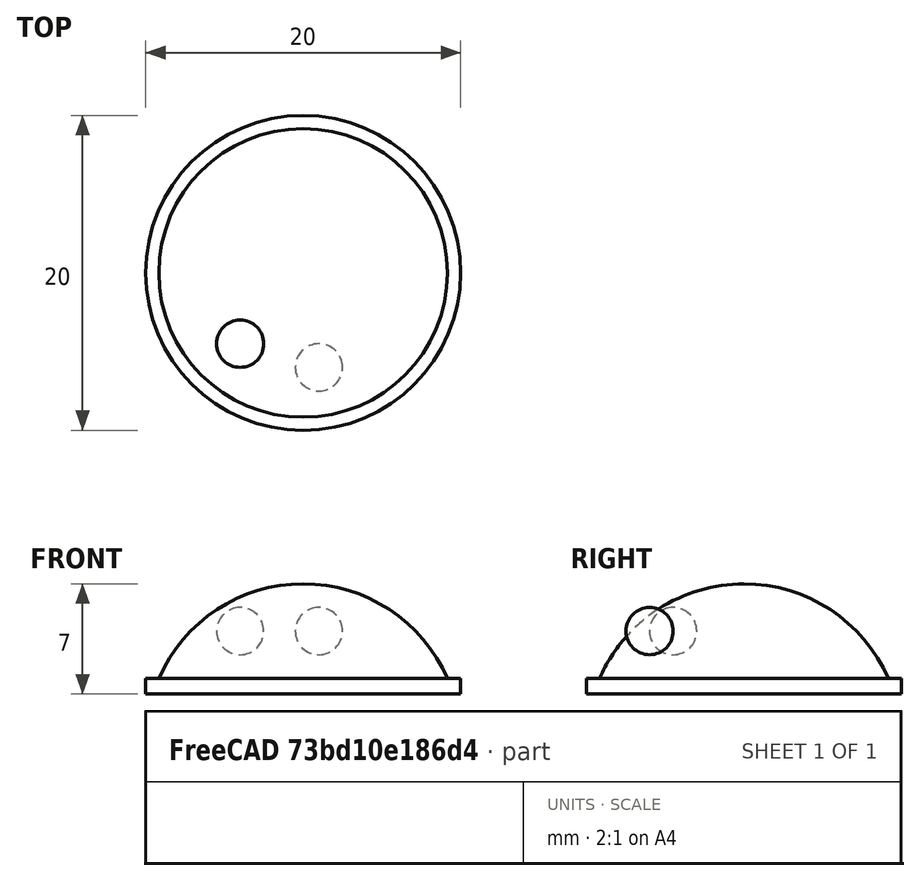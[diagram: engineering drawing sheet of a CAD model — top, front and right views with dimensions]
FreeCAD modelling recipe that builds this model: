
FCSTD DOCUMENT  (FreeCAD 1.0R39319 (Git))
Label: ojt1_t13r01_robot
License: All rights reserved
LicenseURL: https://en.wikipedia.org/wiki/All_rights_reserved
objects: Part::Sphere×3, Part::MultiFuse×2, Part::Cylinder×1
note: 6 computed .brp shape members not serialized (recipe doc carries the construction recipe); baked Part::Feature solids carry a one-line shape summary decoded from their .brp

FEATURE [Part::Sphere] Sphere  label="Esfera"
  Angle1 = 20
  Angle2 = 90
  Angle3 = 360
  AttacherType = Attacher::AttachEngine3D
  Radius = 10
FEATURE [Part::Cylinder] Cylinder  label="Cilindre"
  Angle = 360
  AttacherType = Attacher::AttachEngine3D
  FirstAngle = 0
  Height = 1
  Placement = pos=(0,0,3) rot=(0,0,1;0rad)
  Radius = 10
  SecondAngle = 0
FEATURE [Part::MultiFuse] Fusion
  Refine = true
  Shapes = -> [Sphere,Cylinder]
FEATURE [Part::Sphere] Sphere001  label="Esfera001"
  Angle1 = -90
  Angle2 = 90
  Angle3 = 360
  AttacherType = Attacher::AttachEngine3D
  Placement = pos=(1,-6,7) rot=(0,0,1;0rad)
  Radius = 1.5
FEATURE [Part::Sphere] Sphere002  label="Esfera002"
  Angle1 = -90
  Angle2 = 90
  Angle3 = 360
  AttacherType = Attacher::AttachEngine3D
  Placement = pos=(-4,-4.5,7) rot=(0,0,1;0rad)
  Radius = 1.5
FEATURE [Part::MultiFuse] Fusion001
  Refine = true
  Shapes = -> [Sphere002,Sphere001]
